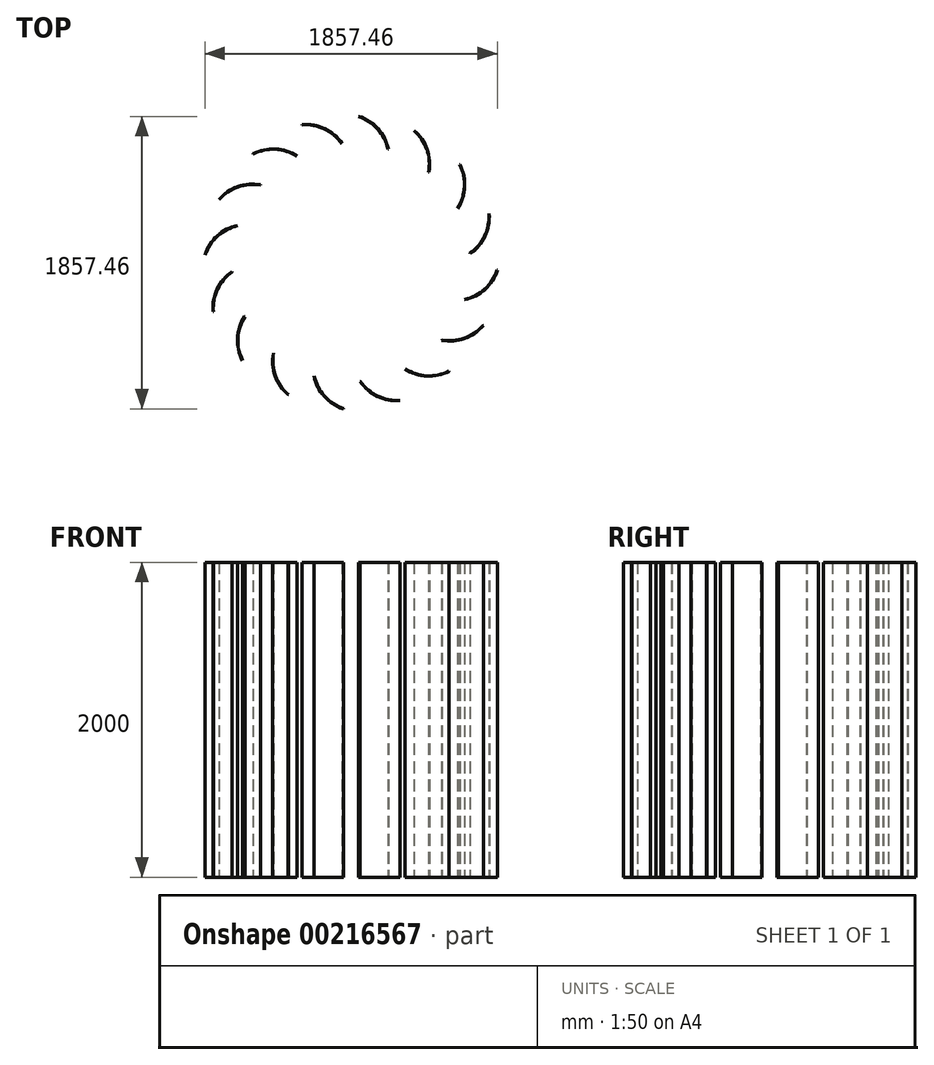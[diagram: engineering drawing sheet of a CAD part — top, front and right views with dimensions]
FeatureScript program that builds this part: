
annotation { "Feature Type Name" : "Feature", "Feature Type Description" : "" }
export const myFeature = defineFeature(function(context is Context, id is Id, definition is map)
    precondition{}
    {
        {
            var Q0;
            Q0=qCreatedBy(makeId("Top.planeOp"),FACE);
            var sketch = newSketch(context, id + "F0", { "sketchPlane" : qUnion([Q0])});
            skCircle(sketch, "E0", {"center": v(0, 0) * mm, "radius": 930 * mm, "construction": true});
            skLineSegment(sketch, "E1", {"start": v(0, 0) * mm, "end": v(-1129.93, 0) * mm, "construction": true});
            skLineSegment(sketch, "E2", {"start": v(-930, 0) * mm, "end": v(-928.07, -0.52) * mm});
            skLineSegment(sketch, "E3", {"start": v(0, 0) * mm, "end": v(-1030.68, 54.02) * mm, "construction": true});
            skPoint(sketch, "E4", {"position": v(-928.73, 48.67) * mm});
            skLineSegment(sketch, "E5", {"start": v(-928.73, 48.67) * mm, "end": v(-578.96, 363.6) * mm, "construction": true});
            skLineSegment(sketch, "E6", {"start": v(-928.73, 48.67) * mm, "end": v(-926.82, 48.05) * mm});
            skCircle(sketch, "E7", {"center": v(-928.73, 48.67) * mm, "radius": 280 * mm, "construction": true});
            skPoint(sketch, "E8", {"position": v(-662.43, -37.85) * mm});
            skPoint(sketch, "E9", {"position": v(-720.64, 236.03) * mm});
            skLineSegment(sketch, "E10", {"start": v(-720.64, 236.03) * mm, "end": v(-720.23, 234.07) * mm});
            skArc(sketch, "E11", {"start": v(-720.64, 236.03) * mm, "mid": v(-849.79, 170.23) * mm, "end": v(-928.73, 48.67) * mm});
            skArc(sketch, "E12", {"start": v(-926.82, 48.05) * mm, "mid": v(-848.45, 168.74) * mm, "end": v(-720.23, 234.07) * mm});
            skLineSegment(sketch, "E13.trimOffspring", {"start": v(-678.03, 35.53) * mm, "end": v(-662.43, -37.85) * mm});
            skLineSegment(sketch, "E14.trimOffspring", {"start": v(-778.93, 0) * mm, "end": v(-328.19, -146.45) * mm});
            skSolve(sketch);
        }
        {
            var Q0;
            Q0=qSketchRegion(id+"F0",true);
            extrude(context, id + "F1", {"entities" : qUnion([Q0]), "depth" : 2000 * mm});
        }
        {
            var Q0;
            Q0=qCreatedBy(makeId("Front.planeOp"),FACE);
            var sketch = newSketch(context, id + "F2", { "sketchPlane" : qUnion([Q0])});
            skLineSegment(sketch, "E15", {"start": v(0, -1523.6) * mm, "end": v(0, 2528.93) * mm, "construction": true});
            skSolve(sketch);
        }
        {
            var Q0;
            Q0=makeQuery(id+"F1.opExtrude","SWEPT_BODY",BODY,{"disambiguationData":[OSD([sQuery(id+"F0.wireOp",EDGE,"E6"),sQuery(id+"F0.wireOp",EDGE,"E10"),sQuery(id+"F0.wireOp",EDGE,"E11"),sQuery(id+"F0.wireOp",EDGE,"E12")])]});
            var Q1;
            Q1=sQuery(id+"F2.wireOp",EDGE,"E15");
            circularPattern(context, id + "F3", {"entities" : qUnion([Q0]), "axis" : qUnion([Q1]), "angle" : 360 * degree, "instanceCount" : 16, "equalSpace" : true});
        }
    });
